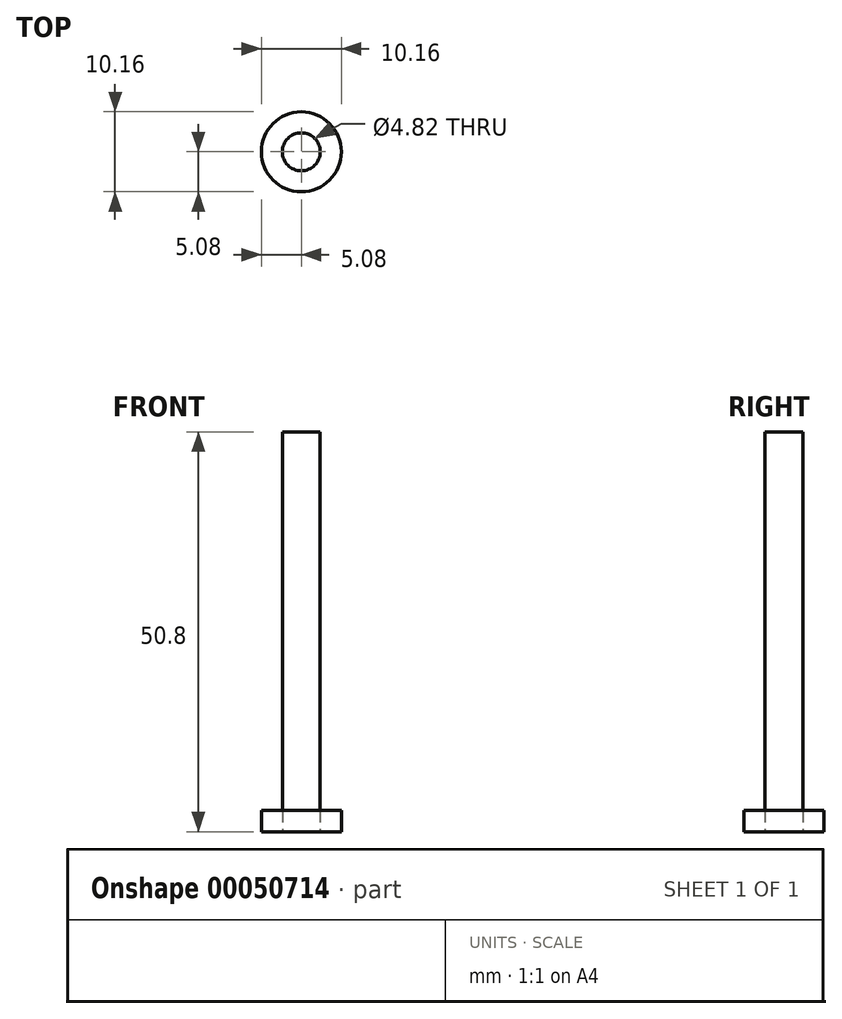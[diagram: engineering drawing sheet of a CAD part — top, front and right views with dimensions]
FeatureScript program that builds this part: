
annotation { "Feature Type Name" : "Feature", "Feature Type Description" : "" }
export const myFeature = defineFeature(function(context is Context, id is Id, definition is map)
    precondition{}
    {
        {
            var Q0;
            Q0=qCreatedBy(makeId("Top.planeOp"),FACE);
            var sketch = newSketch(context, id + "F0", { "sketchPlane" : qUnion([Q0])});
            skCircle(sketch, "E0", {"center": v(0, 0) * mm, "radius": 5.08 * mm});
            skCircle(sketch, "E1", {"center": v(0, 0) * mm, "radius": 2.4 * mm});
            skSolve(sketch);
        }
        {
            var Q0;
            Q0 = qSketchRegion(id + "F0", true);
            extrude(context, id + "F1", {"entities" : qUnion([Q0]), "depth" : 2.7 * mm});
        }
        {
            var Q0;
            Q0=makeQuery(id+"F0.imprint","IMPRINT",FACE,{"disambiguationData":[TD([[makeQuery(id+"F0.imprint","IMPRINT",EDGE,{"derivedFrom":sQuery(id+"F0.wireOp",EDGE,"E1")}),1.0]])]});
            extrude(context, id + "F2", {"entities" : qUnion([Q0]), "depth" : 50.8 * mm});
        }
    });
